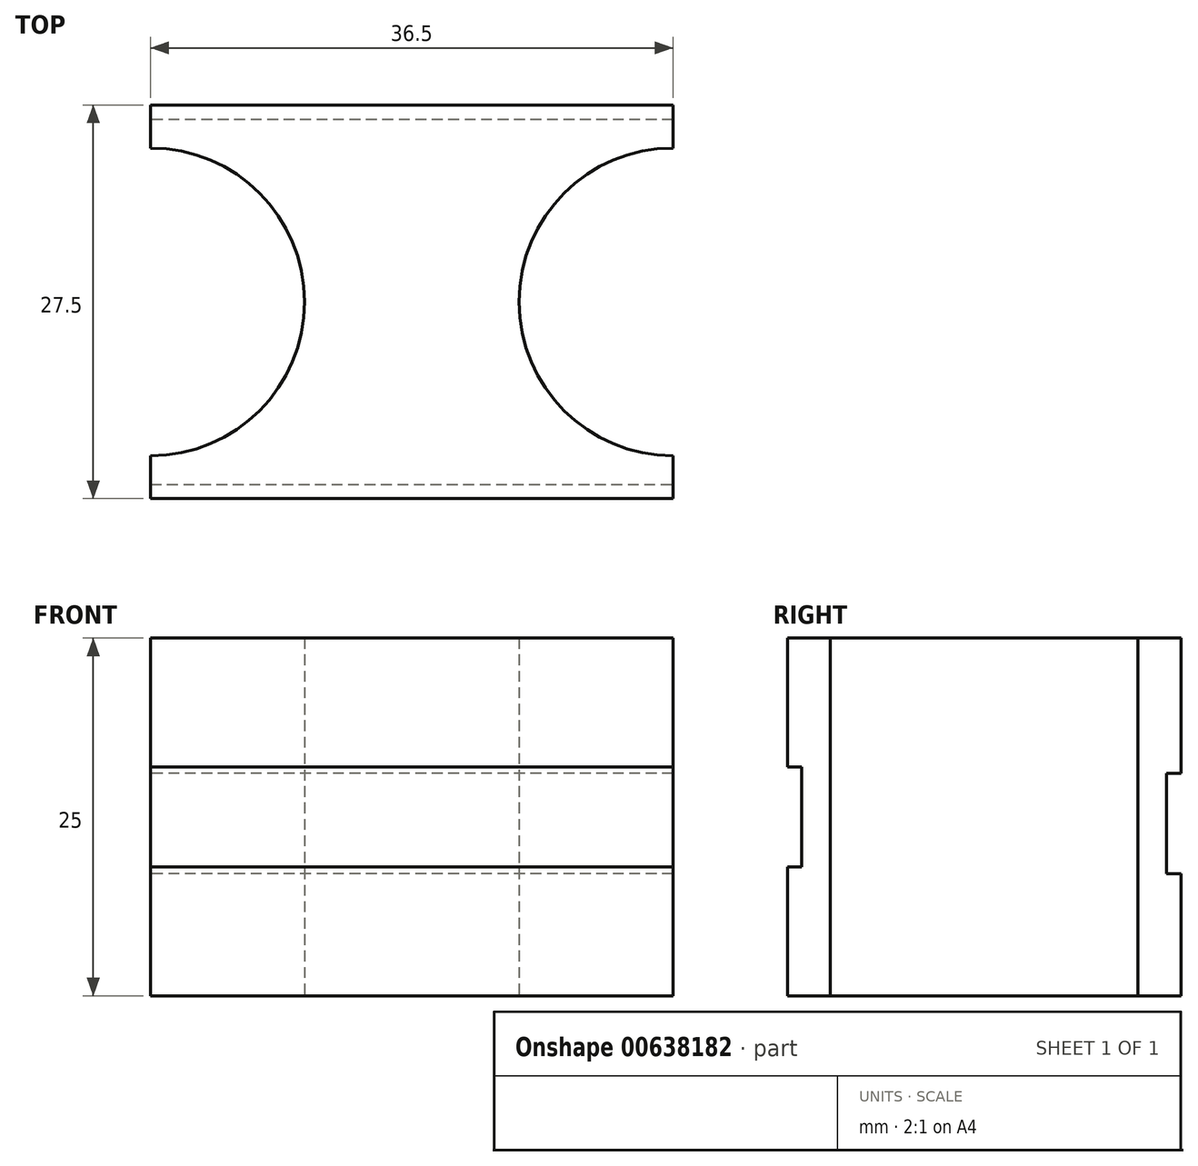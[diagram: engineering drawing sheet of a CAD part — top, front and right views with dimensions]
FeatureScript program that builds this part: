
annotation { "Feature Type Name" : "Feature", "Feature Type Description" : "" }
export const myFeature = defineFeature(function(context is Context, id is Id, definition is map)
    precondition{}
    {
        {
            var Q0;
            Q0=qCreatedBy(makeId("Top.planeOp"),FACE);
            var sketch = newSketch(context, id + "F0", { "sketchPlane" : qUnion([Q0])});
            skCircle(sketch, "E0", {"center": v(19.2, 2.84) * mm, "radius": 10.75 * mm});
            skCircle(sketch, "E1", {"center": v(-17.3, 2.84) * mm, "radius": 10.75 * mm});
            skLineSegment(sketch, "E2.bottom", {"start": v(-17.3, 16.59) * mm, "end": v(19.2, 16.59) * mm});
            skLineSegment(sketch, "E2.top", {"start": v(-17.3, -10.91) * mm, "end": v(19.2, -10.91) * mm});
            skLineSegment(sketch, "E3", {"start": v(-17.3, 16.59) * mm, "end": v(-17.3, 13.59) * mm});
            skLineSegment(sketch, "E4", {"start": v(19.2, 16.59) * mm, "end": v(19.2, 13.59) * mm});
            skLineSegment(sketch, "E5", {"start": v(19.2, -10.91) * mm, "end": v(19.2, -7.91) * mm});
            skLineSegment(sketch, "E6", {"start": v(-17.3, -10.91) * mm, "end": v(-17.3, -7.91) * mm});
            skSolve(sketch);
        }
        {
            var Q0;
            Q0=makeQuery(id+"F0.imprint","IMPRINT",FACE,{"disambiguationData":[TD([[makeQuery(id+"F0.imprint","IMPRINT",EDGE,{"derivedFrom":sQuery(id+"F0.wireOp",EDGE,"E2.bottom")}),-1.0]])]});
            extrude(context, id + "F1", {"entities" : qUnion([Q0]), "depth" : 25 * mm, "offsetDistance" : 25 * mm});
        }
        {
            var Q0;
            Q0=makeQuery(id+"F1.opExtrude","SWEPT_FACE",FACE,{"disambiguationData":[OSD([sQuery(id+"F0.wireOp",EDGE,"E2.top")])]});
            var sketch = newSketch(context, id + "F2", { "sketchPlane" : qUnion([Q0])});
            skLineSegment(sketch, "E7.bottom", {"start": v(-17.3, 16) * mm, "end": v(19.2, 16) * mm});
            skLineSegment(sketch, "E7.top", {"start": v(-17.3, 9) * mm, "end": v(19.2, 9) * mm});
            skLineSegment(sketch, "E7.left", {"start": v(-17.3, 16) * mm, "end": v(-17.3, 9) * mm});
            skLineSegment(sketch, "E7.right", {"start": v(19.2, 16) * mm, "end": v(19.2, 9) * mm});
            skPoint(sketch, "E7.middle", {"position": v(0.95, 12.5) * mm});
            skPoint(sketch, "E7.middle.positionSnap0", {"position": v(0.95, 25) * mm});
            skPoint(sketch, "E7.middle.positionSnap1", {"position": v(-17.3, 12.5) * mm});
            skPoint(sketch, "E7.centerSnap0", {"position": v(0.95, 25) * mm});
            skPoint(sketch, "E7.centerSnap1", {"position": v(-17.3, 12.5) * mm});
            skSolve(sketch);
        }
        {
            var Q0;
            Q0=makeQuery(id+"F2.imprint","IMPRINT",FACE,{"disambiguationData":[TD([[makeQuery(id+"F2.imprint","IMPRINT",EDGE,{"derivedFrom":sQuery(id+"F2.wireOp",EDGE,"E7.bottom")}),-1.0]])]});
            extrude(context, id + "F3", {"entities" : qUnion([Q0]), "operationType" : NewBodyOperationType.REMOVE, "oppositeDirection" : true, "depth" : 1 * mm, "offsetDistance" : 25 * mm});
        }
        {
            var Q0;
            Q0=makeQuery(id+"F1.opExtrude","SWEPT_FACE",FACE,{"disambiguationData":[OSD([sQuery(id+"F0.wireOp",EDGE,"E2.bottom")])]});
            var sketch = newSketch(context, id + "F4", { "sketchPlane" : qUnion([Q0])});
            skLineSegment(sketch, "E8.bottom", {"start": v(-19.2, 15.54) * mm, "end": v(17.3, 15.54) * mm});
            skLineSegment(sketch, "E8.top", {"start": v(-19.2, 8.54) * mm, "end": v(17.3, 8.54) * mm});
            skLineSegment(sketch, "E8.left", {"start": v(-19.2, 15.54) * mm, "end": v(-19.2, 8.54) * mm});
            skLineSegment(sketch, "E8.right", {"start": v(17.3, 15.54) * mm, "end": v(17.3, 8.54) * mm});
            skPoint(sketch, "E8.middle", {"position": v(-0.95, 12.04) * mm});
            skPoint(sketch, "E8.middle.positionSnap0", {"position": v(-0.95, 24.54) * mm});
            skPoint(sketch, "E8.middle.positionSnap1", {"position": v(-19.2, 12.04) * mm});
            skPoint(sketch, "E8.centerSnap0", {"position": v(-0.95, 24.54) * mm});
            skPoint(sketch, "E8.centerSnap1", {"position": v(-19.2, 12.04) * mm});
            skSolve(sketch);
        }
        {
            var Q0;
            Q0=makeQuery(id+"F4.imprint","IMPRINT",FACE,{"disambiguationData":[TD([[makeQuery(id+"F4.imprint","IMPRINT",EDGE,{"derivedFrom":sQuery(id+"F4.wireOp",EDGE,"E8.bottom")}),-1.0]])]});
            extrude(context, id + "F5", {"entities" : qUnion([Q0]), "operationType" : NewBodyOperationType.REMOVE, "oppositeDirection" : true, "depth" : 1 * mm, "offsetDistance" : 25 * mm});
        }
    });
